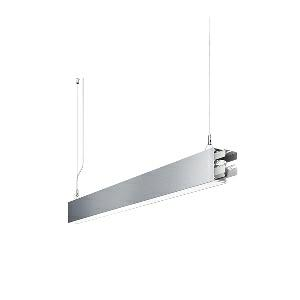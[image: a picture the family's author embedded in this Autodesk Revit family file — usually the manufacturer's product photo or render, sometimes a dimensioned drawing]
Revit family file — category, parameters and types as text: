
# Revit family: idoo_line_-_ilp_2000_840_d_sta_00805683_449d
name_source: partatom
category: Lighting Fixtures
units: mm (PartAtom-declared; Revit-internal decimal feet)

## family parameters
Cut with Voids When Loaded = No
Host = Face
Light Source = No
Part Type = Normal
Room Calculation Point = No
Round Connector Dimension = Use Diameter
Shared = No

## types (1)
- IDOO.line - ILP 2000/840/D STA (1 x LED, 2350 lm, 4000K)
    Apparent Load = 17 VA
    Approval mark = CE
    CIE Flux Codes = 66 91 98 40 100
    Color Rendering = 80-89
    Color Temperature = 4000K
    Control Gear = Electronic ballast
    Default Elevation = 1800 mm
    Description = ILP 2000/840/D|Suspended luminaire|light source: LED|connected load: 220-240 V, 50/60 Hz|Power consumption: approx. 17 W|standby: approx. 0,20|luminous flux: 2350 lm|luminous efficacy: 138 lm/W|light distribution: Direct/indirect|direct ratio: approx. 40 %|colour temperature: Cold white, ca. 4000 K|color rendering index (CRI): >= 80|chromaticity tolerance:  3 SDCM|System of protection: IP 40|technology: Continuously dimmable|luminaire body|material: Sectional aluminium|colour: Silver|lamp cover: Acrylic (PMMA), Clear|mains lead: 2.00 m With free stranded wires|Fastening: Steel cable 0.3 - 0.7 m|glare control: Prism aperture|luminance(L65): <= 2700 cd/m|unified glare rating(4H 8H): <=  16|special features: DALI Load 1x, TouchDIM - dimming via standard switch, Through-wired, up to 18 m on one mains connection, Flicker-free, Suitable as emergency lighting, Start luminaire with mains connection, Mechanical and electrical connection of the individual modules without tools|
    Frequency = 50 Hz
    Height = 110 mm
    Lamp = 1 x LED
    Lamp Light Flux = 2350 lm
    Lamp count = 1
    Length = 848 mm
    Luminous efficacy = 138 lm/W
    Manufacturer = Waldmann
    ModVariant = No
    Model = 00805683
    Mounting Place = Ceiling
    Mounting Type = Pendant
    Number of Poles = 1
    OnlyDefault = Yes
    Power Factor = 1
    Product Name = IDOO.line - ILP 2000/840/D STA
    Product group = Suspended luminaire
    ProductGroupID = 9
    Protection Class = Protection class I
    Protection Degree = IP 40
    RLX_Detail_Level = 1
    RLX_Emergency_Light_Flux = 0 lm
    RLX_Emergency_Type = 0
    RLX_Emergency_Type_DB = No
    RlxData = <blob elided: 20769 chars, md5=f50fc0a1>
    Socket = socket
    Standby Power = 0 W
    System Light Flux = 2350 lm
    System Power = 17 W
    Type Comments = Product without accessories
    Type Image = 113298000-00692558.jpg
    URL = http://relux.com
    VarID = ---
    Voltage = 230 V
    Voltage Range = 220-240 V
    Weight = 0.00 kg
    Width = 60 mm  [stored 0.19685 ft]

note: [stored X ft] marks values corroborated as IEEE doubles in the binary element streams (Revit-internal decimal feet)

## geometry (parser evidence)
native form markers: Blend x4, Sweep x13
no freeform markers — native parametric forms only
